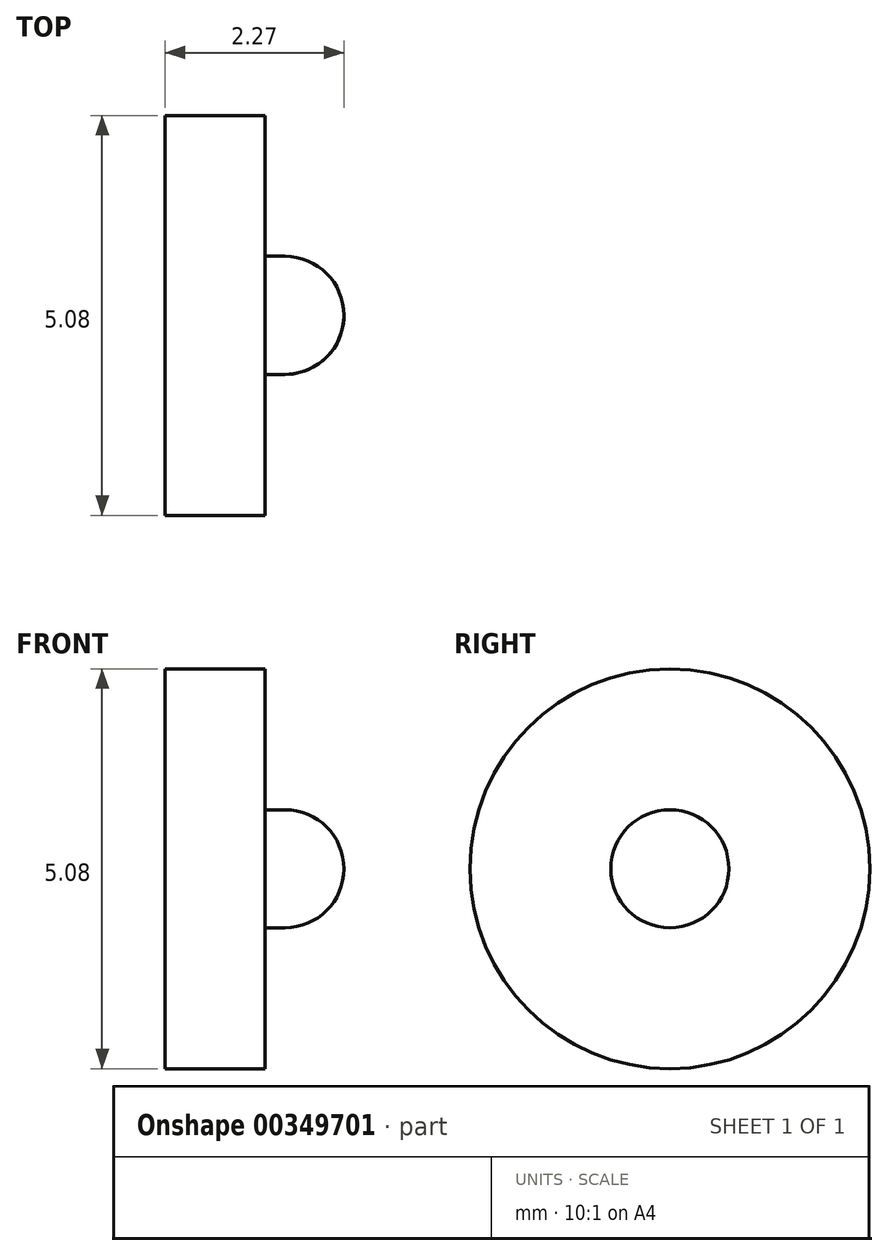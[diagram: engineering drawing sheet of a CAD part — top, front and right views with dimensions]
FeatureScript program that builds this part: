
annotation { "Feature Type Name" : "Feature", "Feature Type Description" : "" }
export const myFeature = defineFeature(function(context is Context, id is Id, definition is map)
    precondition{}
    {
        {
            var Q0;
            Q0=qCreatedBy(makeId("Top.planeOp"),FACE);
            var sketch = newSketch(context, id + "F0", { "sketchPlane" : qUnion([Q0])});
            skLineSegment(sketch, "E0", {"start": v(0, -2.54) * mm, "end": v(0, 0) * mm});
            skLineSegment(sketch, "E1", {"start": v(0, -2.54) * mm, "end": v(1.27, -2.54) * mm});
            skLineSegment(sketch, "E2", {"start": v(1.27, -2.54) * mm, "end": v(1.27, -0.75) * mm});
            skLineSegment(sketch, "E3", {"start": v(1.27, -0.75) * mm, "end": v(1.52, -0.75) * mm});
            skArc(sketch, "E4", {"start": v(1.52, -0.75) * mm, "mid": v(2.05, -0.53) * mm, "end": v(2.27, 0) * mm});
            skLineSegment(sketch, "E5", {"start": v(0, 0) * mm, "end": v(2.27, 0) * mm});
            skSolve(sketch);
        }
        {
            var Q0;
            Q0 = qSketchRegion(id + "F0", true);
            var Q1;
            Q1=sQuery(id+"F0.wireOp",EDGE,"E5");
            revolve(context, id + "F1", {"entities" : qUnion([Q0]), "axis" : qUnion([Q1]), "revolveType" : RevolveType.FULL});
        }
    });
